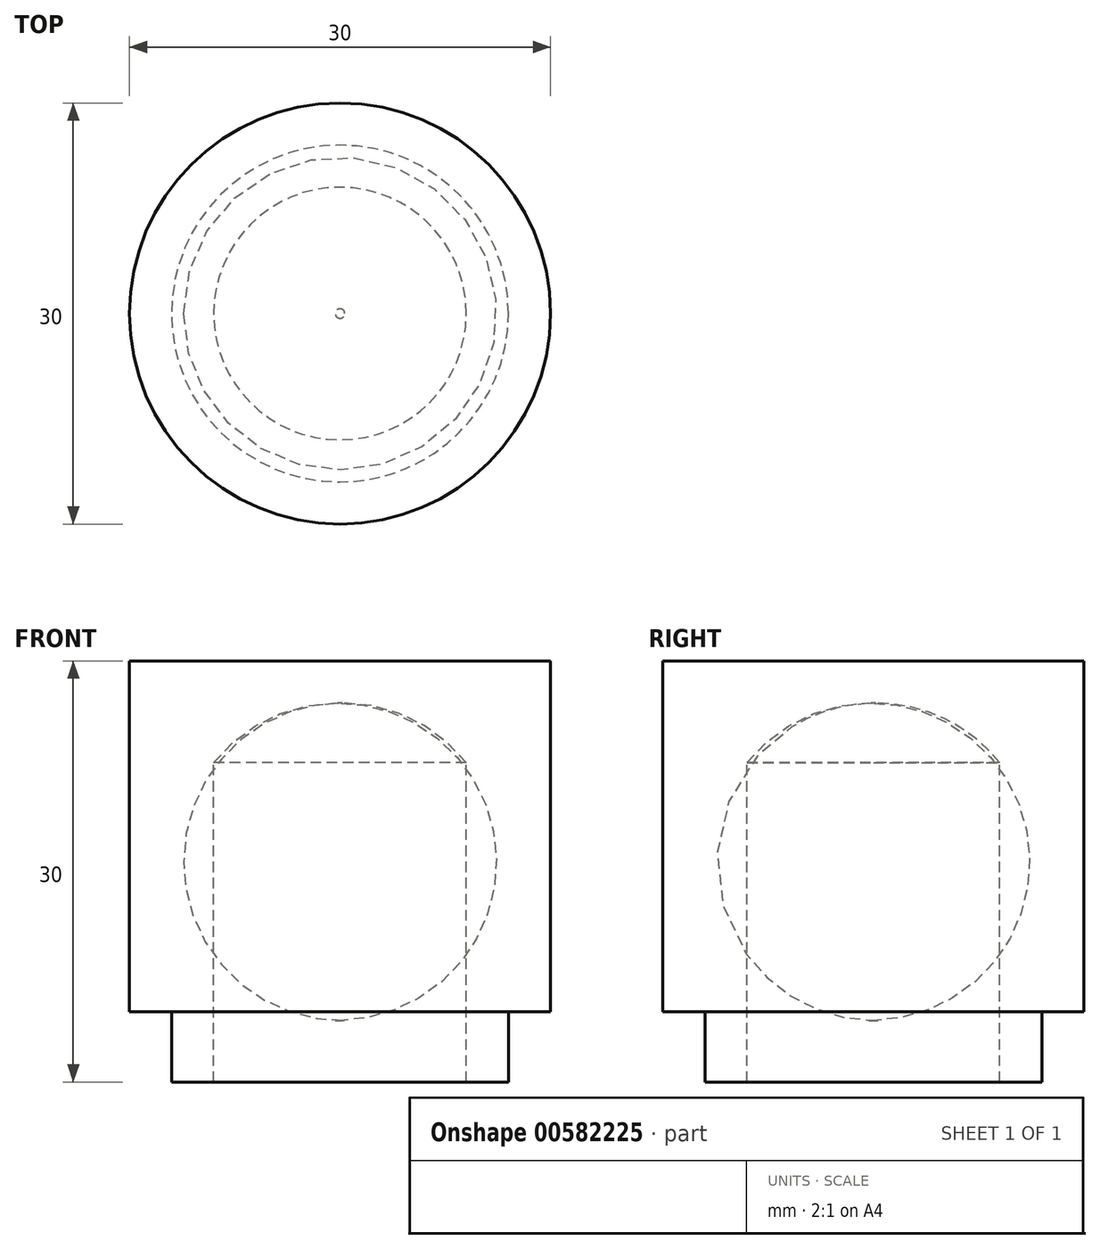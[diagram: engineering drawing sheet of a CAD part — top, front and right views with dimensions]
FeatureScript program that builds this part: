
annotation { "Feature Type Name" : "Feature", "Feature Type Description" : "" }
export const myFeature = defineFeature(function(context is Context, id is Id, definition is map)
    precondition{}
    {
        {
            var Q0;
            Q0=qCreatedBy(makeId("Front.planeOp"),FACE);
            var sketch = newSketch(context, id + "F0", { "sketchPlane" : qUnion([Q0])});
            skLineSegment(sketch, "E0.MirrorCS", {"start": v(-12, -25) * mm, "end": v(-15, -25) * mm});
            skLineSegment(sketch, "E1", {"start": v(-15, -3) * mm, "end": v(-15, 0) * mm});
            skLineSegment(sketch, "E2", {"start": v(-15, -3) * mm, "end": v(-15, -25) * mm});
            skLineSegment(sketch, "E3", {"start": v(-12, -25) * mm, "end": v(-12, -30) * mm});
            skLineSegment(sketch, "E4", {"start": v(-12, -30) * mm, "end": v(-9, -30) * mm});
            skLineSegment(sketch, "E5", {"start": v(-15, 0) * mm, "end": v(0, 0) * mm});
            skLineSegment(sketch, "E6.MirrorCS", {"start": v(12, -25) * mm, "end": v(12, -30) * mm});
            skLineSegment(sketch, "E7.MirrorCS", {"start": v(15, 0) * mm, "end": v(0, 0) * mm});
            skLineSegment(sketch, "E8.MirrorCS", {"start": v(15, -3) * mm, "end": v(15, -25) * mm});
            skLineSegment(sketch, "E9.MirrorCS", {"start": v(12, -25) * mm, "end": v(15, -25) * mm});
            skLineSegment(sketch, "E10.MirrorCS", {"start": v(15, -3) * mm, "end": v(15, 0) * mm});
            skLineSegment(sketch, "E11.MirrorCS", {"start": v(12, -30) * mm, "end": v(9, -30) * mm});
            skArc(sketch, "E12", {"start": v(9, -7.69) * mm, "mid": v(0.11, -3) * mm, "end": v(-9, -7.24) * mm});
            skLineSegment(sketch, "E13", {"start": v(-9, -30) * mm, "end": v(-9, -7.24) * mm});
            skLineSegment(sketch, "E14", {"start": v(9, -30) * mm, "end": v(9, -7.69) * mm});
            skLineSegment(sketch, "E15", {"start": v(0, 0) * mm, "end": v(0, -3) * mm});
            skSolve(sketch);
        }
        {
            var Q0;
            {var subQ0=sQuery(id+"F0.wireOp",EDGE,"I7DhDJuf-7NLr-Svl4-PwQn-US4yEfDLbxPE.left");Q0=makeQuery(id+"F0.imprint","IMPRINT",FACE,{"disambiguationData":[TD([[makeQuery(id+"F0.imprint","IMPRINT",EDGE,{"derivedFrom":subQ0}),-1.0]])]});}
            var Q1;
            Q1=makeQuery(id+"F0.imprint","IMPRINT",FACE,{"disambiguationData":[TD([[makeQuery(id+"F0.imprint","IMPRINT",EDGE,{"derivedFrom":sQuery(id+"F0.wireOp",EDGE,"32eac864-653d-4b33-877a-62f6442f8a590.MirrorCS")}),1.0]])]});
            var Q2;
            Q2=makeQuery(id+"F0.imprint","IMPRINT",FACE,{"disambiguationData":[TD([[makeQuery(id+"F0.imprint","IMPRINT",EDGE,{"derivedFrom":sQuery(id+"F0.wireOp",EDGE,"E0.MirrorCS")}),-1.0]])]});
            var Q3;
            Q3=sQuery(id+"F0.wireOp",EDGE,"E15");
            revolve(context, id + "F1", {"entities" : qUnion([Q0, Q1, Q2]), "axis" : qUnion([Q3]), "revolveType" : RevolveType.FULL});
        }
    });
